# Revit family: Versailles 600
name_source: partatom
category: Lighting Fixtures
revit_build: Autodesk Revit 2018 (Build: 20170223_1515(x64)
units: mm (PartAtom-declared; Revit-internal decimal feet)

## family parameters
Always vertical = Yes
Cut with Voids When Loaded = No
Host = Wall
Light Source = Yes
OmniClass Number = 23.80.70.00
OmniClass Title = Lighting
Part Type = Normal
Room Calculation Point = No
Round Connector Dimension = Use Diameter
Shared = No

## types (2) — shared parameters
Color Filter = 16777215
Dimmable = No
Dimming Lamp Color Temperature Shift = <None>
Driver Included = Yes
Driver Required = No
Efficacy (lm/w) = 43
Electrical Class = 2
Emit from Line Length = 610 mm
Lamp = LED
Location rating = IP44
Main Finish = Polished Chrome
Main Material = Metal - Steel
Manufacturer = Astro Lighting Ltd
Photometric Web File = GNC-21589 Versailles 600 Bronze - 8482 inc sphere.ies
Power (Watts) = 25.0
Product Location = Bathroom
Tilt Angle = 60.00°
URL = www.astrolighting.com

## per-type parameters (varying)
| type | Product Code | Product Name | Product SKU |
| Polished Chrome | 8482 | Versailles 600 LED - Polished Chrome | 1380011 |
| Bronze | 8483 | Versailles 600 LED - Bronze | 1380012 |

## geometry (parser evidence)
native form markers: Sweep x1
no freeform markers — native parametric forms only
